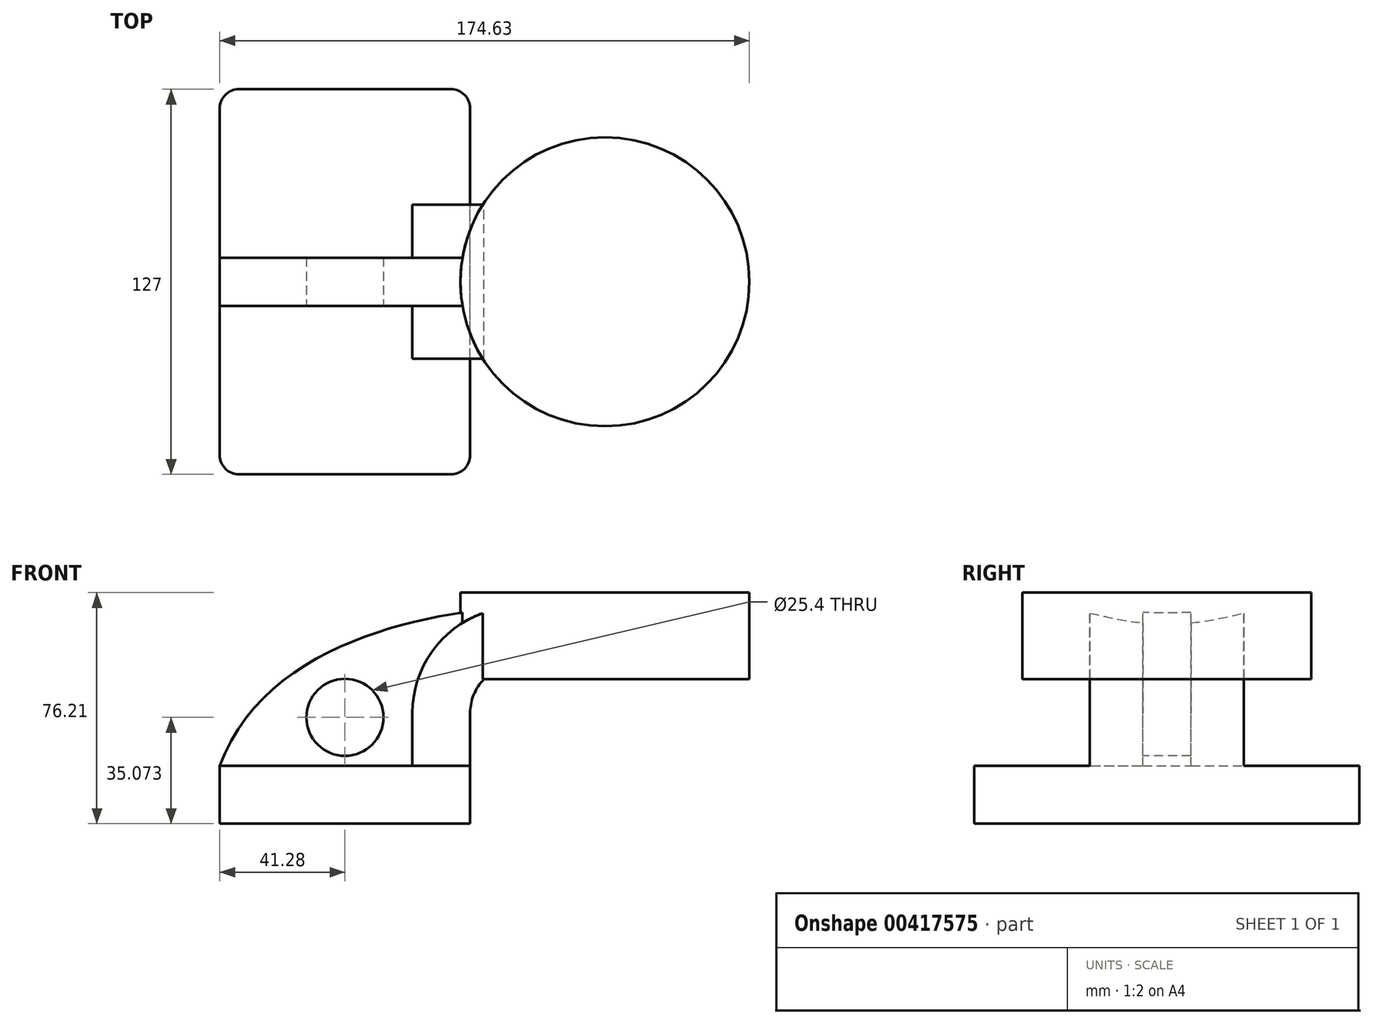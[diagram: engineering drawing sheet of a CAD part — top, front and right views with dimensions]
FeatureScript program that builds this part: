
annotation { "Feature Type Name" : "Feature", "Feature Type Description" : "" }
export const myFeature = defineFeature(function(context is Context, id is Id, definition is map)
    precondition{}
    {
        {
            var Q0;
            Q0=qCreatedBy(makeId("Front.planeOp"),FACE);
            var sketch = newSketch(context, id + "F0", { "sketchPlane" : qUnion([Q0])});
            skLineSegment(sketch, "E0.bottom", {"start": v(-41.28, 9.52) * mm, "end": v(41.28, 9.52) * mm});
            skLineSegment(sketch, "E0.top", {"start": v(-41.28, -9.52) * mm, "end": v(41.28, -9.52) * mm});
            skLineSegment(sketch, "E0.left", {"start": v(-41.28, 9.52) * mm, "end": v(-41.28, -9.52) * mm});
            skLineSegment(sketch, "E0.right", {"start": v(41.28, 9.52) * mm, "end": v(41.28, -9.52) * mm});
            skPoint(sketch, "E0.middle", {"position": v(0, 0) * mm});
            skLineSegment(sketch, "E1", {"start": v(41.28, 9.53) * mm, "end": v(41.28, 27) * mm});
            skLineSegment(sketch, "E2.bottom", {"start": v(133.35, 66.68) * mm, "end": v(57.15, 66.68) * mm});
            skLineSegment(sketch, "E2.top", {"start": v(133.35, 38.1) * mm, "end": v(57.15, 38.1) * mm});
            skLineSegment(sketch, "E2.left", {"start": v(133.35, 66.68) * mm, "end": v(133.35, 38.1) * mm});
            skLineSegment(sketch, "E2.right", {"start": v(57.15, 66.68) * mm, "end": v(57.15, 38.1) * mm});
            skPoint(sketch, "E2.middle", {"position": v(95.25, 52.39) * mm});
            skArc(sketch, "E3", {"start": v(41.28, 27) * mm, "mid": v(45.92, 38.23) * mm, "end": v(57.15, 42.88) * mm});
            skLineSegment(sketch, "E4", {"start": v(57.15, 42.88) * mm, "end": v(85.73, 42.88) * mm});
            skLineSegment(sketch, "E5.0", {"start": v(57.15, 61.93) * mm, "end": v(85.73, 61.93) * mm});
            skArc(sketch, "E5.1", {"start": v(22.23, 27) * mm, "mid": v(32.45, 51.7) * mm, "end": v(57.15, 61.93) * mm});
            skLineSegment(sketch, "E5.2", {"start": v(22.23, 9.53) * mm, "end": v(22.23, 27) * mm});
            skLineSegment(sketch, "E6", {"start": v(85.73, 42.88) * mm, "end": v(85.73, 61.93) * mm});
            skFitSpline(sketch, "E7", {"points": [v(-41.28, 9.52) * mm, v(57.15, 61.93) * mm, v(85.73, 61.93) * mm], "startDerivative": vector(67.57, 188.58) * mm, "endDerivative": vector(74.66, 6.7) * mm});
            skLineSegment(sketch, "E8", {"start": v(85.73, 61.93) * mm, "end": v(85.73, 66.68) * mm});
            skLineSegment(sketch, "E9", {"start": v(85.73, 66.68) * mm, "end": v(85.73, 38.1) * mm});
            skSolve(sketch);
        }
        {
            var Q0;
            Q0=makeQuery(id+"F0.imprint","IMPRINT",FACE,{"disambiguationData":[TD([[makeQuery(id+"F0.imprint","IMPRINT",EDGE,{"derivedFrom":sQuery(id+"F0.wireOp",EDGE,"E0.top")}),1.0]])]});
            extrude(context, id + "F1", {"entities" : qUnion([Q0]), "endBound" : BoundingType.SYMMETRIC, "depth" : 127 * mm});
        }
        {
            var Q0;
            {var subQ1=sQuery(id+"F0.wireOp",EDGE,"E1");Q0=makeQuery(id+"F0.imprint","IMPRINT",FACE,{"disambiguationData":[TD([[makeQuery(id+"F0.imprint","IMPRINT",EDGE,{"derivedFrom":subQ1}),1.0]])]});}
            var Q1;
            {var subQ6=sQuery(id+"F0.wireOp",EDGE,"E4");Q1=makeQuery(id+"F0.imprint","IMPRINT",FACE,{"disambiguationData":[TD([[makeQuery(id+"F0.imprint","IMPRINT",EDGE,{"derivedFrom":subQ6}),1.0]])]});}
            extrude(context, id + "F2", {"entities" : qUnion([Q0, Q1]), "operationType" : NewBodyOperationType.ADD, "endBound" : BoundingType.SYMMETRIC, "depth" : 50.8 * mm});
        }
        {
            var Q0;
            {var subQ3=sQuery(id+"F0.wireOp",EDGE,"E5.2");Q0=makeQuery(id+"F0.imprint","IMPRINT",FACE,{"disambiguationData":[TD([[makeQuery(id+"F0.imprint","IMPRINT",EDGE,{"derivedFrom":subQ3}),1.0]])]});}
            extrude(context, id + "F3", {"entities" : qUnion([Q0]), "operationType" : NewBodyOperationType.ADD, "endBound" : BoundingType.SYMMETRIC, "depth" : 15.88 * mm});
        }
        {
            var Q0;
            {var subQ4=sQuery(id+"F0.wireOp",EDGE,"E2.left");Q0=makeQuery(id+"F0.imprint","IMPRINT",FACE,{"disambiguationData":[TD([[makeQuery(id+"F0.imprint","IMPRINT",EDGE,{"derivedFrom":subQ4}),-1.0]])]});}
            var Q1;
            Q1=sQuery(id+"F0.wireOp",EDGE,"E9");
            revolve(context, id + "F4", {"operationType" : NewBodyOperationType.ADD, "entities" : qUnion([Q0]), "axis" : qUnion([Q1]), "revolveType" : RevolveType.FULL});
        }
        {
            var Q0;
            Q0=makeQuery(id+"F1.opExtrude","CAP_EDGE",EDGE,{"disambiguationData":[OSD([sQuery(id+"F0.wireOp",EDGE,"E0.right")])],"isStart":false});
            var Q1;
            Q1=makeQuery(id+"F1.opExtrude","CAP_EDGE",EDGE,{"disambiguationData":[OSD([sQuery(id+"F0.wireOp",EDGE,"E0.left")])],"isStart":false});
            var Q2;
            Q2=makeQuery(id+"F1.opExtrude","CAP_EDGE",EDGE,{"disambiguationData":[OSD([sQuery(id+"F0.wireOp",EDGE,"E0.left")])],"isStart":true});
            var Q3;
            Q3=makeQuery(id+"F1.opExtrude","CAP_EDGE",EDGE,{"disambiguationData":[OSD([sQuery(id+"F0.wireOp",EDGE,"E0.right")])],"isStart":true});
            fillet(context, id + "F5", {"entities" : qUnion([Q0, Q1, Q2, Q3]), "radius" : 6.35 * mm, "tangentPropagation" : true, "allowEdgeOverflow" : false});
        }
        {
            var Q0;
            Q0=makeQuery(id+"F3.opExtrude","CAP_FACE",FACE,{"disambiguationData":[OSD([sQuery(id+"F0.wireOp",EDGE,"E0.bottom"),sQuery(id+"F0.wireOp",EDGE,"E5.1"),sQuery(id+"F0.wireOp",EDGE,"E5.2"),sQuery(id+"F0.wireOp",EDGE,"E7")])],"isStart":false});
            var sketch = newSketch(context, id + "F6", { "sketchPlane" : qUnion([Q0])});
            skCircle(sketch, "E10", {"center": v(0, 25.54) * mm, "radius": 12.7 * mm});
            skSolve(sketch);
        }
        {
            var Q0;
            Q0=makeQuery(id+"F6.imprint","IMPRINT",FACE,{"disambiguationData":[TD([[makeQuery(id+"F6.imprint","IMPRINT",EDGE,{"derivedFrom":sQuery(id+"F6.wireOp",EDGE,"E10")}),1.0]])]});
            extrude(context, id + "F7", {"entities" : qUnion([Q0]), "operationType" : NewBodyOperationType.REMOVE, "oppositeDirection" : true, "depth" : 50.8 * mm});
        }
    });
